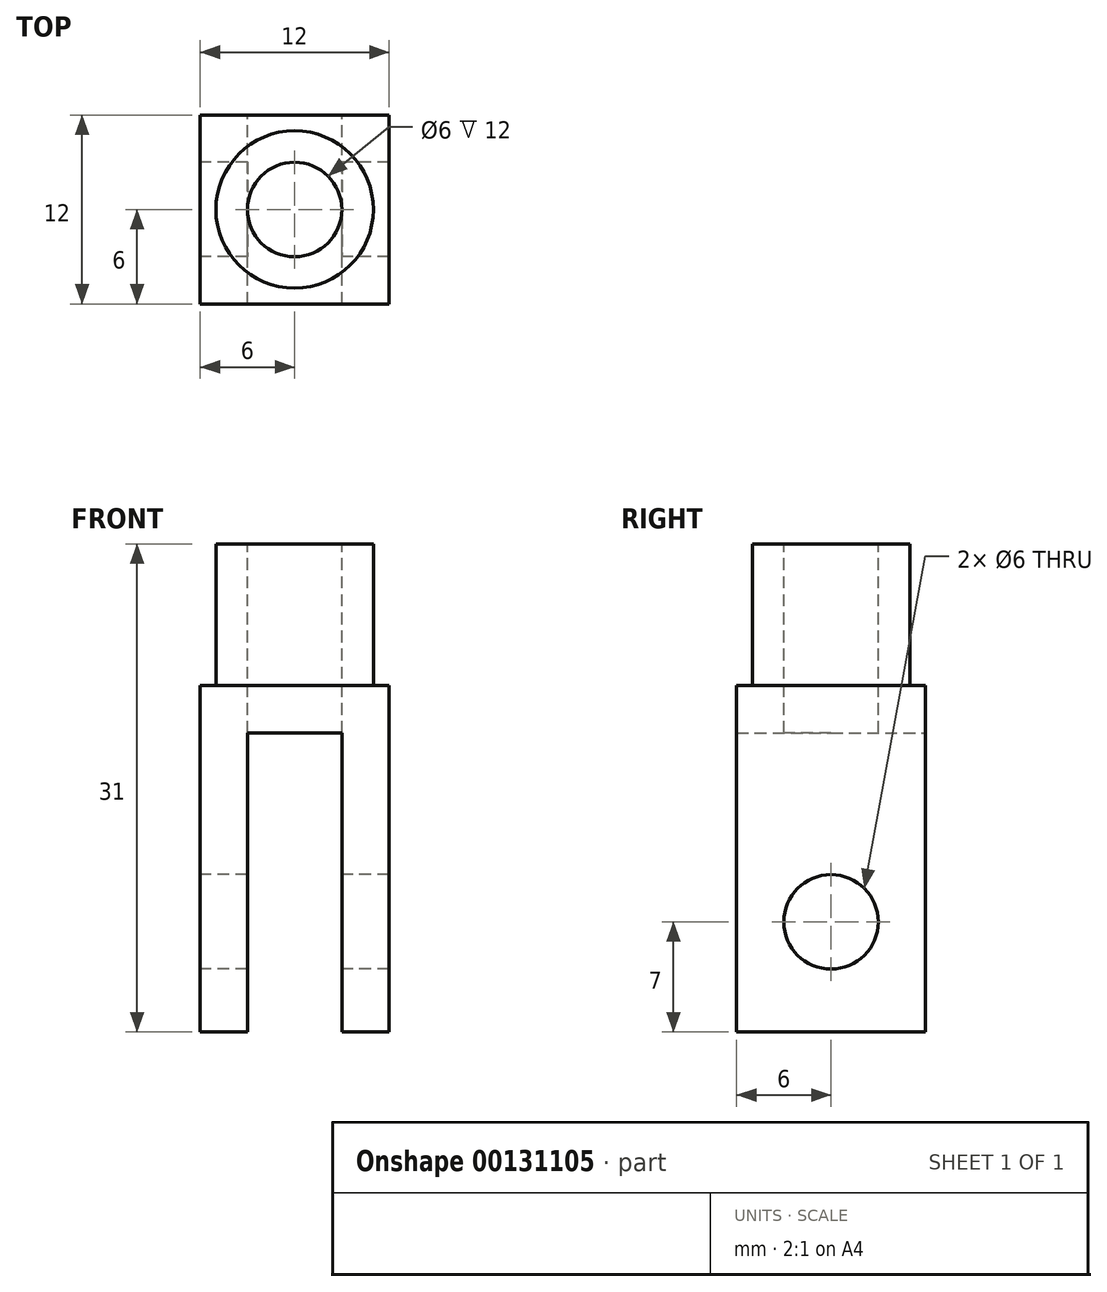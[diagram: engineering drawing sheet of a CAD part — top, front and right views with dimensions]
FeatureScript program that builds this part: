
annotation { "Feature Type Name" : "Feature", "Feature Type Description" : "" }
export const myFeature = defineFeature(function(context is Context, id is Id, definition is map)
    precondition{}
    {
        {
            var Q0;
            Q0=qCreatedBy(makeId("Front.planeOp"),FACE);
            var sketch = newSketch(context, id + "F0", { "sketchPlane" : qUnion([Q0])});
            skLineSegment(sketch, "E0.bottom", {"start": v(6, -11) * mm, "end": v(3, -11) * mm});
            skLineSegment(sketch, "E0.top", {"start": v(6, 11) * mm, "end": v(-6, 11) * mm});
            skLineSegment(sketch, "E0.left", {"start": v(6, -11) * mm, "end": v(6, 11) * mm});
            skLineSegment(sketch, "E0.right", {"start": v(-6, -11) * mm, "end": v(-6, 11) * mm});
            skPoint(sketch, "E0.middle", {"position": v(0, 0) * mm});
            skPoint(sketch, "E1", {"position": v(0, 8) * mm});
            skLineSegment(sketch, "E2.left", {"start": v(3, -11) * mm, "end": v(3, 8) * mm});
            skLineSegment(sketch, "E2.right", {"start": v(-3, -11) * mm, "end": v(-3, 8) * mm});
            skLineSegment(sketch, "E3", {"start": v(3, 8) * mm, "end": v(-3, 8) * mm});
            skPoint(sketch, "E4.orphan", {"position": v(-3, 11) * mm});
            skPoint(sketch, "E5.orphan", {"position": v(3, 11) * mm});
            skLineSegment(sketch, "E6.trimOffspring", {"start": v(-3, -11) * mm, "end": v(-6, -11) * mm});
            skSolve(sketch);
        }
        {
            var Q0;
            Q0=makeQuery(id+"F0.imprint","IMPRINT",FACE,{"disambiguationData":[TD([[makeQuery(id+"F0.imprint","IMPRINT",EDGE,{"derivedFrom":sQuery(id+"F0.wireOp",EDGE,"E0.bottom")}),-1.0]])]});
            extrude(context, id + "F1", {"entities" : qUnion([Q0]), "depth" : 12 * mm});
        }
        {
            var Q0;
            Q0=makeQuery(id+"F1.opExtrude","SWEPT_FACE",FACE,{"disambiguationData":[OSD([sQuery(id+"F0.wireOp",EDGE,"E0.top")])]});
            var sketch = newSketch(context, id + "F2", { "sketchPlane" : qUnion([Q0])});
            skCircle(sketch, "E7", {"center": v(0, -6) * mm, "radius": 5 * mm});
            skPoint(sketch, "E7.centerSnap0", {"position": v(6, -6) * mm});
            skPoint(sketch, "E7.centerSnap1", {"position": v(0, -12) * mm});
            skSolve(sketch);
        }
        {
            var Q0;
            Q0=makeQuery(id+"F2.imprint","IMPRINT",FACE,{"disambiguationData":[TD([[makeQuery(id+"F2.imprint","IMPRINT",EDGE,{"derivedFrom":sQuery(id+"F2.wireOp",EDGE,"E7")}),1.0]])]});
            extrude(context, id + "F3", {"entities" : qUnion([Q0]), "operationType" : NewBodyOperationType.ADD, "depth" : 9 * mm});
        }
        {
            var Q0;
            Q0=makeQuery(id+"F3.opExtrude","CAP_FACE",FACE,{"disambiguationData":[OSD([sQuery(id+"F2.wireOp",EDGE,"E7")])],"isStart":false});
            var sketch = newSketch(context, id + "F4", { "sketchPlane" : qUnion([Q0])});
            skPoint(sketch, "E8", {"position": v(0, -6) * mm});
            skSolve(sketch);
        }
        {
            var Q0;
            Q0=sQuery(id+"F4.wireOp",VERTEX,"E8");
            var Q1;
            Q1=makeQuery(id+"F1.opExtrude","SWEPT_BODY",BODY,{"disambiguationData":[OSD([sQuery(id+"F0.wireOp",EDGE,"E0.bottom"),sQuery(id+"F0.wireOp",EDGE,"E0.top"),sQuery(id+"F0.wireOp",EDGE,"E0.left"),sQuery(id+"F0.wireOp",EDGE,"E0.right"),sQuery(id+"F0.wireOp",EDGE,"E2.left"),sQuery(id+"F0.wireOp",EDGE,"E2.right"),sQuery(id+"F0.wireOp",EDGE,"E3"),sQuery(id+"F0.wireOp",EDGE,"E6.trimOffspring")])]});
            hole(context, id + "F5", {"style" : HoleStyle.SIMPLE, "endStyle" : HoleEndStyle.THROUGH, "holeDiameter" : 6 * mm, "locations" : qUnion([Q0]), "scope" : qUnion([Q1]), "isTappedThrough" : true});
        }
        {
            var Q0;
            Q0=makeQuery(id+"F1.opExtrude","SWEPT_FACE",FACE,{"disambiguationData":[OSD([sQuery(id+"F0.wireOp",EDGE,"E0.right")])]});
            var sketch = newSketch(context, id + "F6", { "sketchPlane" : qUnion([Q0])});
            skPoint(sketch, "E9", {"position": v(6, -4) * mm});
            skPoint(sketch, "E9.positionSnap0", {"position": v(6, -11) * mm});
            skSolve(sketch);
        }
        {
            var Q0;
            Q0=sQuery(id+"F6.wireOp",VERTEX,"E9");
            var Q1;
            Q1=makeQuery(id+"F1.opExtrude","SWEPT_BODY",BODY,{"disambiguationData":[OSD([sQuery(id+"F0.wireOp",EDGE,"E0.bottom"),sQuery(id+"F0.wireOp",EDGE,"E0.top"),sQuery(id+"F0.wireOp",EDGE,"E0.left"),sQuery(id+"F0.wireOp",EDGE,"E0.right"),sQuery(id+"F0.wireOp",EDGE,"E2.left"),sQuery(id+"F0.wireOp",EDGE,"E2.right"),sQuery(id+"F0.wireOp",EDGE,"E3"),sQuery(id+"F0.wireOp",EDGE,"E6.trimOffspring")])]});
            var Q2;
            Q2=makeQuery(id+"F1.opExtrude","SWEPT_BODY",BODY,{"disambiguationData":[OSD([sQuery(id+"F0.wireOp",EDGE,"E0.bottom"),sQuery(id+"F0.wireOp",EDGE,"E0.top"),sQuery(id+"F0.wireOp",EDGE,"E0.left"),sQuery(id+"F0.wireOp",EDGE,"E0.right"),sQuery(id+"F0.wireOp",EDGE,"E2.left"),sQuery(id+"F0.wireOp",EDGE,"E2.right"),sQuery(id+"F0.wireOp",EDGE,"E3"),sQuery(id+"F0.wireOp",EDGE,"E6.trimOffspring")])]});
            hole(context, id + "F7", {"style" : HoleStyle.SIMPLE, "endStyle" : HoleEndStyle.THROUGH, "holeDiameter" : 6 * mm, "locations" : qUnion([Q0]), "scope" : qUnion([Q1, Q2]), "isTappedThrough" : true});
        }
    });
